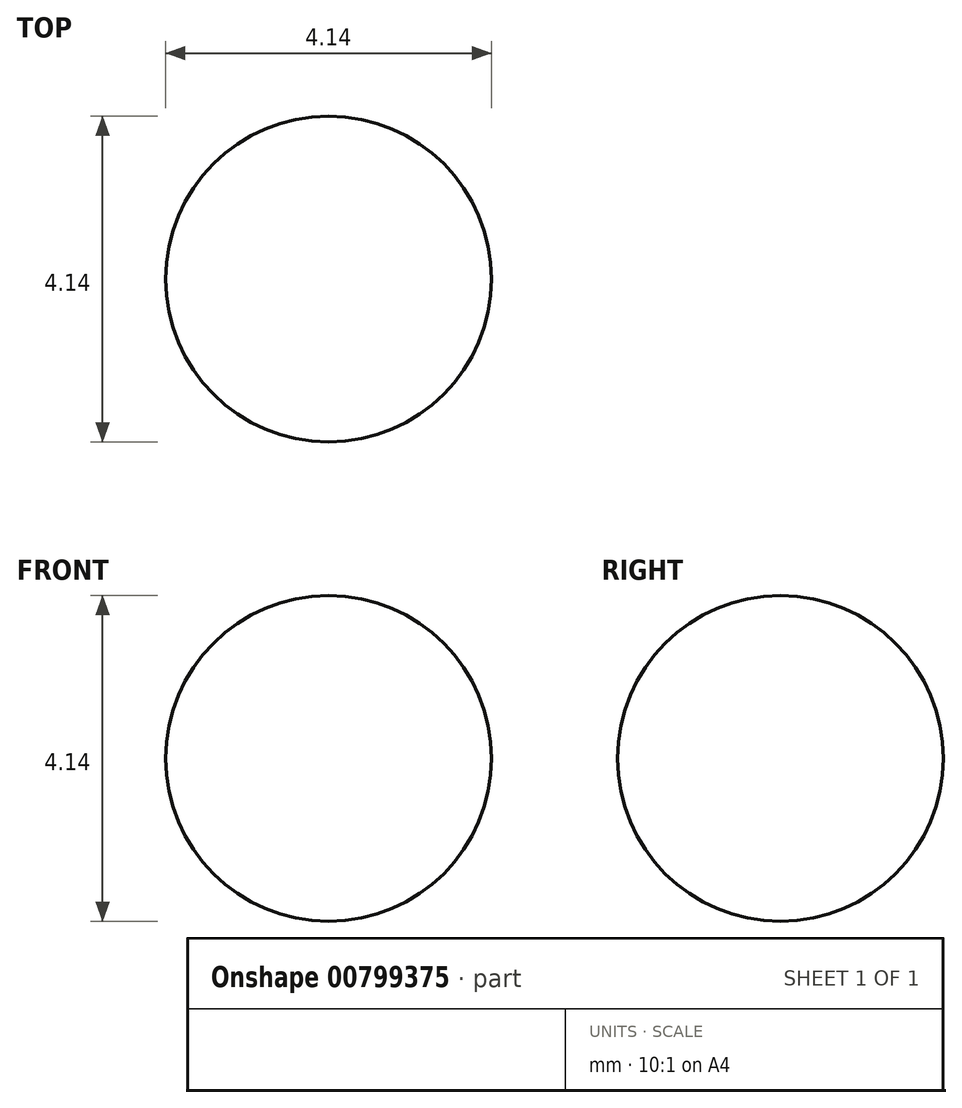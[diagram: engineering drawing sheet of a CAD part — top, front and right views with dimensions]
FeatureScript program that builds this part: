
annotation { "Feature Type Name" : "Feature", "Feature Type Description" : "" }
export const myFeature = defineFeature(function(context is Context, id is Id, definition is map)
    precondition{}
    {
        {
            var Q0;
            Q0=qCreatedBy(makeId("Right.planeOp"),FACE);
            var sketch = newSketch(context, id + "F0", { "sketchPlane" : qUnion([Q0])});
            skArc(sketch, "E0", {"start": v(0, -2.07) * mm, "mid": v(2.07, 0) * mm, "end": v(0, 2.07) * mm});
            skLineSegment(sketch, "E1", {"start": v(0, 2.07) * mm, "end": v(0, -2.07) * mm});
            skSolve(sketch);
        }
        {
            var Q0;
            Q0=sQuery(id+"F0.wireOp",EDGE,"E0");
            var Q1;
            Q1=sQuery(id+"F0.wireOp",EDGE,"E1");
            revolve(context, id + "F1", {"bodyType" : ExtendedToolBodyType.SURFACE, "surfaceOperationType" : NewSurfaceOperationType.NEW, "surfaceEntities" : qUnion([Q0]), "axis" : qUnion([Q1]), "revolveType" : RevolveType.FULL});
        }
    });
